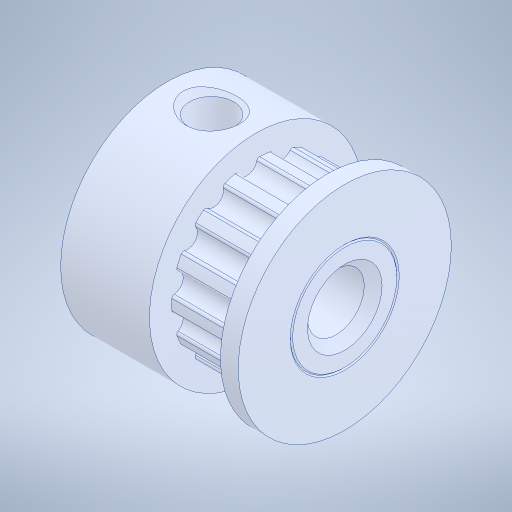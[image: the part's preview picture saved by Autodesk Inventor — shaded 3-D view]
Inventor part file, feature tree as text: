
AUTODESK INVENTOR PART (.ipt)
format: ipt  version: 2023.2 (Build 272271000, 271)  size: 350,720 bytes
history: mixed  units: in
note: dims shown in document units (in); Inventor stores cm internally (conversion verified against a paired STEP export)
features: other x2, chamfer x1, imported_body x1
ambient origin geometry x8: Origin, YZ Plane, XZ Plane, XY Plane, X Axis, Y Axis, Z Axis, Center Point
bodies: Solid1 (imported_parasolid)
feature tree (4):
  other  "belt horizontal midplane"
  other  "SET SCREW PLANE"
  chamfer  "Chamfer1"  [1 undecoded]
  imported_body  NMx_Import_Brep_tag  [imported B-rep: ~68 faces, bbox_mm=[10.0, 7.872413, 12.0]]
note: 1 required parameter value undecoded (feature->parameter linkage not recoverable at this tier; creation-order binding heuristic only, values carry confidence <= 0.55)
